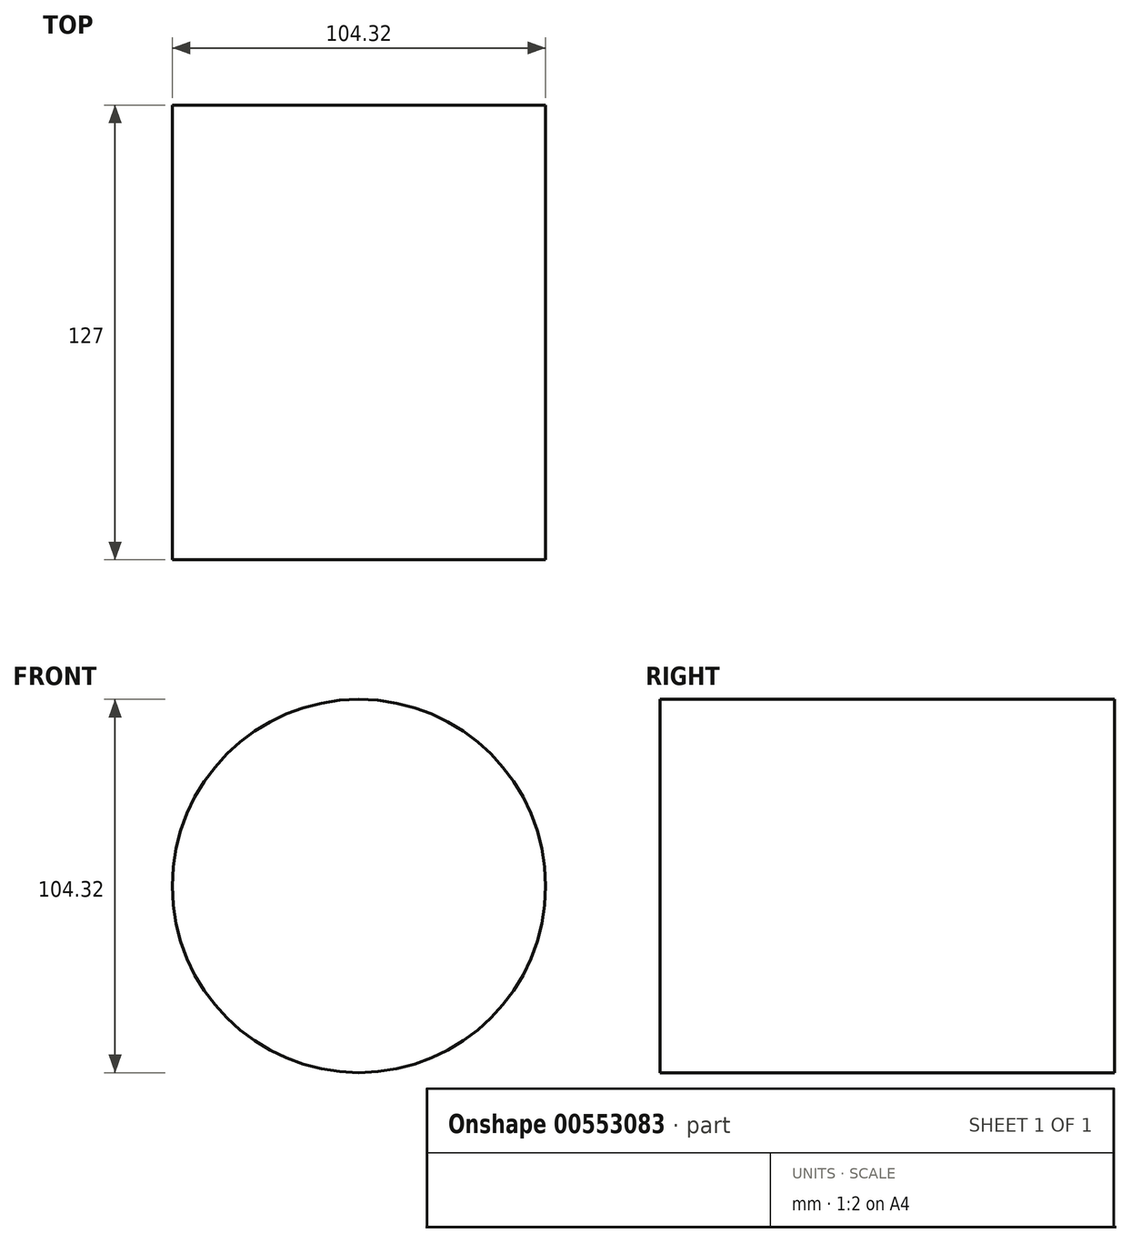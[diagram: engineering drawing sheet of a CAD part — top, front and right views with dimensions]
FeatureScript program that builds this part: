
annotation { "Feature Type Name" : "Feature", "Feature Type Description" : "" }
export const myFeature = defineFeature(function(context is Context, id is Id, definition is map)
    precondition{}
    {
        {
            var Q0;
            Q0=qCreatedBy(makeId("Front.planeOp"),FACE);
            var sketch = newSketch(context, id + "F0", { "sketchPlane" : qUnion([Q0])});
            skCircle(sketch, "E0", {"center": v(0, 0) * mm, "radius": 52.16 * mm});
            skSolve(sketch);
        }
        {
            var Q0;
            Q0=makeQuery(id+"F0.imprint","IMPRINT",FACE,{"disambiguationData":[TD([[makeQuery(id+"F0.imprint","IMPRINT",EDGE,{"derivedFrom":sQuery(id+"F0.wireOp",EDGE,"E0")}),1.0]])]});
            extrude(context, id + "F1", {"entities" : qUnion([Q0]), "endBound" : BoundingType.SYMMETRIC, "depth" : 127 * mm, "offsetDistance" : 25.4 * mm});
        }
    });
